# Revit family: НЕВАТОМ_Вентилятор VKRS-Е (3,15-10)_240619
name_source: partatom
category: Оборудование
units: mm (PartAtom-declared; Revit-internal decimal feet)

## family parameters
Всегда вертикально = Да
На основе рабочей плоскости = Нет
Общий = Нет
При загрузке вырезать с полостями = Нет
Размер круглого соединителя = Использовать диаметр
Тип детали = Нормальный
Точка расчета площади = Нет

## types (11) — shared parameters
ADSK_Единица измерения = шт.
ADSK_Завод-изготовитель = НЕВАТОМ
ADSK_Коэффициент мощности = 1
ADSK_Материал наименование = Оцинкованная сталь
ADSK_Наименование = Вентилятор крышный радиальный с выбросом в сторону
ADSK_Напряжение = 380 В
ADSK_Полная мощность = 0 В·А
ADSK_Потеря давления воздуха = 0.0 Па
ADSK_Расход воздуха = 0 м³/ч
Nevatom_URL = https://t.me
h = 20 мм
Ключевая пометка = Вентиляция
Материал = Сталь ASTM A441

## per-type parameters (varying)
- VKRS № 4,0: ADSK_Марка=VKRS-Е-4,0; ADSK_Масса=71; ADSK_Размер_Высота=820 мм; ADSK_Размер_Длина=625 мм; ADSK_Размер_Ширина=625 мм; ADSK_Ток=11 А; ADSK_Частота вращения вентилятора=3000; B=530 мм; D=400 мм; H=820 мм; H1=492 мм; H2=418 мм; H3=467 мм; L=625 мм; L1=830 мм; L1-100=730 мм; h1=25 мм; h6=41 мм; l=525 мм; l1=263 мм; l2=315 мм; l3=446 мм; l4=650 мм; n=2; Мощность двигателя N, кВт=6 кВт; Н6=205 мм; Н7=117 мм
- VKRS № 4,5: ADSK_Марка=VKRS-Е-4,5; ADSK_Масса=82.8; ADSK_Размер_Высота=1010 мм; ADSK_Размер_Длина=655 мм; ADSK_Размер_Ширина=655 мм; ADSK_Ток=1 А; ADSK_Частота вращения вентилятора=1000; B=580 мм; D=450 мм; H=1010 мм; H1=606 мм; H2=515 мм; H3=576 мм; L=655 мм; L1=844 мм; L1-100=744 мм; h1=30 мм; h6=51 мм; l=555 мм; l1=278 мм; l2=333 мм; l3=472 мм; l4=664 мм; n=2; Мощность двигателя N, кВт=0 кВт; Н6=253 мм; Н7=144 мм
- VKRS № 5,6: ADSK_Марка=VKRS-Е-5,6; ADSK_Масса=109; ADSK_Размер_Высота=930 мм; ADSK_Размер_Длина=765 мм; ADSK_Размер_Ширина=765 мм; ADSK_Ток=3 А; ADSK_Частота вращения вентилятора=1000; B=690 мм; D=560 мм; H=930 мм; H1=558 мм; H2=474 мм; H3=530 мм; L=765 мм; L1=1000 мм; L1-100=900 мм; h1=28 мм; h6=47 мм; l=665 мм; l1=333 мм; l2=399 мм; l3=565 мм; l4=820 мм; n=2; Мощность двигателя N, кВт=1 кВт; Н6=233 мм; Н7=133 мм
- VKRS № 7,1: ADSK_Марка=VKRS-Е-7,1; ADSK_Масса=190.9; ADSK_Размер_Высота=1310 мм; ADSK_Размер_Длина=920 мм; ADSK_Размер_Ширина=920 мм; ADSK_Ток=6 А; ADSK_Частота вращения вентилятора=750; B=840 мм; D=710 мм; H=1310 мм; H1=786 мм; H2=668 мм; H3=747 мм; L=920 мм; L1=1190 мм; L1-100=1090 мм; h1=39 мм; h6=66 мм; l=820 мм; l1=410 мм; l2=492 мм; l3=697 мм; l4=1010 мм; n=2; Мощность двигателя N, кВт=2 кВт; Н6=328 мм; Н7=187 мм
- VKRS № 3,15: ADSK_Марка=VKRS-Е-3,15; ADSK_Масса=49.8; ADSK_Размер_Высота=665 мм; ADSK_Размер_Длина=555 мм; ADSK_Размер_Ширина=555 мм; ADSK_Ток=0 А; ADSK_Частота вращения вентилятора=1500; B=440 мм; D=315 мм; H=665 мм; H1=399 мм; H2=339 мм; H3=379 мм; L=555 мм; L1=720 мм; L1-100=620 мм; h1=20 мм; h6=33 мм; l=455 мм; l1=228 мм; l2=273 мм; l3=387 мм; l4=540 мм; n=2; Мощность двигателя N, кВт=0 кВт; Н6=166 мм; Н7=95 мм
- VKRS № 3,55: ADSK_Марка=VKRS-Е-3,55; ADSK_Масса=62.7; ADSK_Размер_Высота=755 мм; ADSK_Размер_Длина=555 мм; ADSK_Размер_Ширина=555 мм; ADSK_Ток=1 А; ADSK_Частота вращения вентилятора=3000; B=480 мм; D=355 мм; H=755 мм; H1=453 мм; H2=385 мм; H3=430 мм; L=555 мм; L1=765 мм; L1-100=665 мм; h1=23 мм; h6=38 мм; l=455 мм; l1=228 мм; l2=273 мм; l3=387 мм; l4=585 мм; n=2; Мощность двигателя N, кВт=0 кВт; Н6=189 мм; Н7=108 мм
- VKRS № 5,0: ADSK_Марка=VKRS-Е-5,0; ADSK_Масса=93.8; ADSK_Размер_Высота=855 мм; ADSK_Размер_Длина=710 мм; ADSK_Размер_Ширина=710 мм; ADSK_Ток=1 А; ADSK_Частота вращения вентилятора=1000; B=630 мм; D=500 мм; H=855 мм; H1=513 мм; H2=436 мм; H3=487 мм; L=710 мм; L1=950 мм; L1-100=850 мм; h1=26 мм; h6=43 мм; l=610 мм; l1=305 мм; l2=366 мм; l3=519 мм; l4=770 мм; n=2; Мощность двигателя N, кВт=0 кВт; Н6=214 мм; Н7=122 мм
- VKRS № 6,3: ADSK_Марка=VKRS-Е-6,3; ADSK_Масса=139; ADSK_Размер_Высота=1150 мм; ADSK_Размер_Длина=850 мм; ADSK_Размер_Ширина=850 мм; ADSK_Ток=9 А; ADSK_Частота вращения вентилятора=1500; B=754 мм; D=630 мм; H=1150 мм; H1=690 мм; H2=587 мм; H3=656 мм; L=850 мм; L1=1085 мм; L1-100=985 мм; h1=35 мм; h6=58 мм; l=750 мм; l1=375 мм; l2=450 мм; l3=638 мм; l4=905 мм; n=4; Мощность двигателя N, кВт=4 кВт; Н6=288 мм; Н7=164 мм
- VKRS № 8,0: ADSK_Марка=VKRS-Е-8,0; ADSK_Масса=274; ADSK_Размер_Высота=1635 мм; ADSK_Размер_Длина=1080 мм; ADSK_Размер_Ширина=1080 мм; ADSK_Ток=9 А; ADSK_Частота вращения вентилятора=1000; B=1005 мм; D=800 мм; H=1635 мм; H1=981 мм; H2=834 мм; H3=932 мм; L=1080 мм; L1=1300 мм; L1-100=1200 мм; h1=49 мм; h6=82 мм; l=980 мм; l1=490 мм; l2=588 мм; l3=833 мм; l4=1120 мм; n=2; Мощность двигателя N, кВт=4 кВт; Н6=409 мм; Н7=234 мм
- VKRS № 10,0: ADSK_Марка=VKRS-Е-10,0; ADSK_Масса=462.7; ADSK_Размер_Высота=1830 мм; ADSK_Размер_Длина=1315 мм; ADSK_Размер_Ширина=1315 мм; ADSK_Ток=14 А; ADSK_Частота вращения вентилятора=750; B=1180 мм; D=1000 мм; H=1830 мм; H1=1098 мм; H2=933 мм; H3=1043 мм; L=1315 мм; L1=1540 мм; L1-100=1440 мм; h1=55 мм; h6=92 мм; l=1215 мм; l1=608 мм; l2=729 мм; l3=1033 мм; l4=1360 мм; n=2; Мощность двигателя N, кВт=6 кВт; Н6=458 мм; Н7=261 мм
- VKRS № 9,0: ADSK_Марка=VKRS-Е-9,0; ADSK_Масса=386.7; ADSK_Размер_Высота=1710 мм; ADSK_Размер_Длина=1080 мм; ADSK_Размер_Ширина=1080 мм; ADSK_Ток=9 А; ADSK_Частота вращения вентилятора=1000; B=1005 мм; D=800 мм; H=1710 мм; H1=1026 мм; H2=872 мм; H3=975 мм; L=1080 мм; L1=1425 мм; L1-100=1325 мм; h1=51 мм; h6=86 мм; l=980 мм; l1=490 мм; l2=588 мм; l3=833 мм; l4=1245 мм; n=2; Мощность двигателя N, кВт=4 кВт; Н6=428 мм; Н7=244 мм
